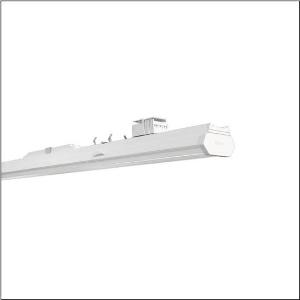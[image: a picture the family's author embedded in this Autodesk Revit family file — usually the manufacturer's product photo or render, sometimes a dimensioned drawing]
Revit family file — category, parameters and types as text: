
# Revit family: licross_r__21_protected_ho_52td12dn4e5m3c_ce33
name_source: partatom
category: Lighting Fixtures
units: mm (PartAtom-declared; Revit-internal decimal feet)

## family parameters
Cut with Voids When Loaded = No
Host = Face
Light Source = No
Part Type = Normal
Room Calculation Point = No
Round Connector Dimension = Use Diameter
Shared = No

## types (1)
- --- (1 x LED, 910 lm, 7.6 W, 4000K)
    Apparent Load = 8 VA
    CIE Flux Codes = 70 91 97 98 100
    Color Rendering = 80
    Color Temperature = 4000K
    Default Elevation = 1800 mm
    Description = Licross® 21 Protected HO, luminaire insert, of sheet steel, galvanised, coil coated, white, length: 1.500mm, width: 90mm, height: 103mm, LED rated luminous flux: 14.690lm, light colour: 840, control gear: DALI 2, with plug, 6-pole, with phase selection, for trunking rail, 14-core, mains connection: 220..240V, AC, 50/60Hz, rated input power: 89W, for trunking rail, 14-core, halogen-free wiring, for emergency light function, converter,control gear: single battery element, battery: LiFeP04, 9Ah, primary light control with lens, of plastic, primary optical cover: cover, of PMMA, light emission: direct distribution, primary light characteristic: symmetric, protection rating (complete): IP54, insulation class (complete): insulation class I (protective earthing), certification: CE, UKCA, protection symbol: D if used in an environment with non-conductive dust loads with corresponding accessories, impact resistance: IK06, permissible ambient temperature for indoor applications: +5..+30°C, standard: EN 60598-2-22, LABS conformity tested according to VDMA 24364:2018-05, reducing of maximum allowable ambient temperature of 5°C with ceiling mounting, corresponds to IFS (International Featured Standards) requirements for safety and quality in the food industry, packaging unit: 1 piece
    Height = 92 mm
    Lamp = 1 x LED
    Lamp Light Flux = 910 lm
    Lamp Power = 7.6 W
    Lamp count = 1
    Length = 1500 mm
    Luminous efficacy = 120 lm/W
    Manufacturer = Siteco
    ModVariant = No
    Model = 52TD12DN4E5M3C
    Mounting Place = Ceiling
    Mounting Type = Pendant
    Number of Poles = 1
    OnlyDefault = Yes
    Power Factor = 1
    Product Name = Licross® 21 Protected HO
    Product group = luminaire insert
    ProductGroupID = 901
    Protection Class = Protection class I
    Protection Degree = IP 54
    RLX_Detail_Level = 1
    RLX_Emergency_Light_Flux = 0 lm
    RLX_Emergency_Type = 0
    RLX_Emergency_Type_DB = No
    RlxData = <blob elided: 24929 chars, md5=325a930e>
    Socket = socket
    Standby Power = 0 W
    System Light Flux = 910 lm
    System Power = 8 W
    Type Comments = : emergency light operation: 3 h
    Type Image = l_1256148.jpg
    URL = http://relux.com
    VarID = @adj_041311
    Voltage = 0 V
    Weight = 0.00 kg
    Width = 88 mm

## geometry (parser evidence)
native form markers: Blend x4, Sweep x11
no freeform markers — native parametric forms only
